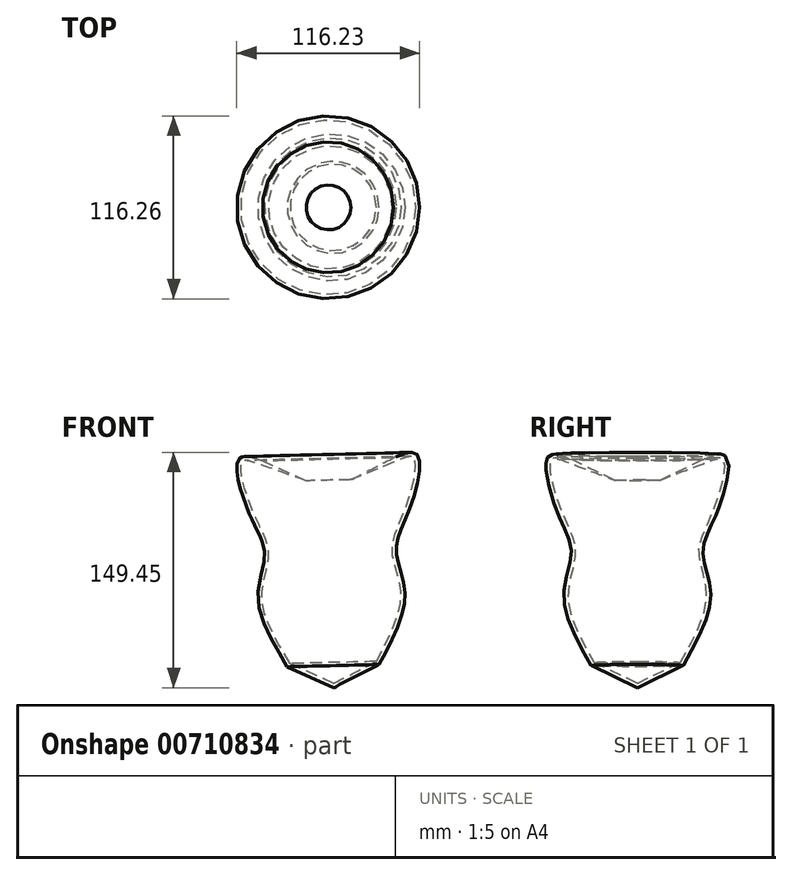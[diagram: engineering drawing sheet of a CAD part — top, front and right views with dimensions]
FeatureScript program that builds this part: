
annotation { "Feature Type Name" : "Feature", "Feature Type Description" : "" }
export const myFeature = defineFeature(function(context is Context, id is Id, definition is map)
    precondition{}
    {
        {
            var Q0;
            Q0=qCreatedBy(makeId("Front.planeOp"),FACE);
            var sketch = newSketch(context, id + "F0", { "sketchPlane" : qUnion([Q0])});
            skLineSegment(sketch, "E0", {"start": v(-3.16, 71.38) * mm, "end": v(0, -53.5) * mm});
            skLineSegment(sketch, "E1", {"start": v(0, -53.5) * mm, "end": v(28.85, -38.73) * mm});
            skFitSpline(sketch, "E2", {"points": [v(28.85, -38.73) * mm, v(45.3, 5.81) * mm, v(39.6, 33.47) * mm, v(47.64, 58.72) * mm, v(53.01, 94.53) * mm, v(37.91, 92.5) * mm], "startDerivative": vector(98.8, 184.28) * mm, "endDerivative": vector(-130.87, -53.98) * mm});
            skLineSegment(sketch, "E3", {"start": v(37.91, 92.5) * mm, "end": v(-3.16, 71.38) * mm});
            skSolve(sketch);
        }
        {
            var Q0;
            Q0=makeQuery(id+"F0.imprint","IMPRINT",FACE,{"disambiguationData":[TD([[makeQuery(id+"F0.imprint","IMPRINT",EDGE,{"derivedFrom":sQuery(id+"F0.wireOp",EDGE,"E0")}),1.0]])]});
            var Q1;
            Q1=sQuery(id+"F0.wireOp",EDGE,"E0");
            revolve(context, id + "F1", {"surfaceOperationType" : NewSurfaceOperationType.NEW, "entities" : qUnion([Q0]), "axis" : qUnion([Q1]), "revolveType" : RevolveType.FULL});
        }
        {
            var Q0;
            Q0=makeQuery(id+"F1.opRevolve","SWEPT_FACE",FACE,{"disambiguationData":[OSD([sQuery(id+"F0.wireOp",EDGE,"E3")])]});
            shell(context, id + "F2", {"entities" : qUnion([Q0]), "thickness" : 2.54 * mm});
        }
    });
